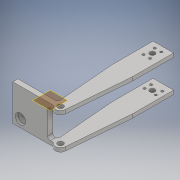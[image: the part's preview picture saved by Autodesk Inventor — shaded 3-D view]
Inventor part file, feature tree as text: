
AUTODESK INVENTOR PART (.ipt)
format: ipt  version: 2017 (Build 210142000, 142)  size: 246,784 bytes
history: native  units: in
note: dims shown in document units (in); Inventor stores cm internally (conversion verified against a paired STEP export)
features: sketch x9, projected_geometry x9, hole x5, extrude x4, plane x2, fillet x2
ambient origin geometry x8: Origin, YZ Plane, XZ Plane, XY Plane, X Axis, Y Axis, Z Axis, Center Point
bodies: Solid1 (feature_tree)
feature tree (31):
  sketch  "Sketch1"  dims[d0=5.0in d1=1.0in]
  plane  "Work Plane1"
  extrude  "Extrusion2"  Depth=1.0in
  plane  "Work Plane2"
  extrude  "Extrusion3"  Depth=0.5in
  hole  "Hole2"  [1 undecoded]
  extrude  "Extrusion4"  Depth=0.5in
  extrude  "Extrusion5"  Depth=1.753in
  fillet  "Fillet1"  Radius=2.0in
  fillet  "Fillet2"  Radius=1.753in
  hole  "Hole3"  [1 undecoded]
  hole  "Hole4"  [1 undecoded]
  hole  "Hole5"  [1 undecoded]
  hole  "Hole6"  [1 undecoded]
  sketch  "Sketch2"  dims[d5=1.0in d6=0.5in]
  projected_geometry  "Projected Loop1"
  sketch  "Sketch4"  dims[d7=0.5in d8=0.0in]
  projected_geometry  "Projected Loop3"
  sketch  "Sketch5"  dims[d9=1.753in d10=0.0in d18=0.5in]
  projected_geometry  "Projected Loop4"
  sketch  "Sketch8"  dims[d19=0.25in d20=2.0in d21=2.0in d22=1.753in d23=0.0in]
  projected_geometry  "Projected Loop9"
  projected_geometry  "Projected Loop10"
  sketch  "Sketch9"  dims[d24=0.27in d25=0.75in d26=0.375in d27=0.25in d28=0.5635in d29=1.0in d30=0.8108in d31=2.0in]
  projected_geometry  "Projected Loop11"
  sketch  "Sketch10"  dims[d32=0.25in d35=5.0in]
  projected_geometry  "Projected Loop12"
  sketch  "Sketch11"  dims[d36=4.875in d37=1.753in d38=0.0in]
  projected_geometry  "Projected Loop13"
  sketch  "Sketch12"  dims[d41=1.753in d42=5.375in d43=1.378in d44=0.1875in d45=5.875in d46=1.0in d47=0.0in d48=0.125in d49=0.125in d50=0.6299in d51=1.0in d52=0.5in d53=0.315in d54=0.1575in d55=0.117in d56=0.75in d57=0.375in d58=0.25in d59=0.5635in d60=1.0in d61=0.8108in d62=0.6299in d63=1.0in d64=0.5in d65=0.315in d66=0.1575in d67=0.117in d68=0.75in d69=0.375in d70=0.25in d71=0.5635in d72=1.0in d73=0.8108in d74=0.375in d75=1.753in d77=0.5in d78=0.75in d79=0.375in d80=0.25in d81=0.5635in d82=0.125in d83=0.8108in d84=1.0in d85=0.5in d86=0.5455in d87=0.2728in d88=0.25in d89=0.75in d90=0.375in d91=0.25in d92=0.5635in d93=1.0in d94=0.8108in d95=0.27in d96=0.1975in d97=0.375in]
  projected_geometry  "Projected Loop14"
note: 5 required parameter values undecoded (feature->parameter linkage not recoverable at this tier; creation-order binding heuristic only, values carry confidence <= 0.55)
